# Revit family: Thorn Voyager Solid
name_source: partatom
category: Lighting Fixtures
revit_build: Autodesk Revit 2016 (Build: 20150220_1215(x64)
units: mm (PartAtom-declared; Revit-internal decimal feet)

## family parameters
Cut with Voids When Loaded = No
Host = Face
Light Source = Yes
OmniClass Number = 23.80.70.11
OmniClass Title = Luminaries for Internal Lighting
Part Type = Normal
Room Calculation Point = No
Round Connector Dimension = Use Diameter
Shared = No

## types (2) — shared parameters
Apparent Load = 2 VA
Assembly Code = D5020200
Body = Thorn_Metal_Light_Grey
Color Filter = 16777215
Cover = Thorn_PMMA_Semitransparent
Description = LED surface mount luminaire
Dimming Lamp Color Temperature Shift = <None>
Emit Shape Visible in Rendering = No
Height = 71 mm
Lamp = LED
Manufacturer = Thorn Lighting
Photometric Web File = 96629766_(STD).IES
Tilt Angle = -90.00°
Voltage = 230 V
zero-valued in all types: Default Elevation

## per-type parameters (varying)
| type | Emit from Rectangle Length | Emit from Rectangle Width | Length | Model | URL | Width |
| VOYAGER Solid L | 150 mm | 360 mm  [stored 1.1811 ft] | 360 mm  [stored 1.1811 ft] | 96629766 | www.thornlighting.com/96629766 | 150 mm |
| VOYAGER Solid MS | 130 mm  [stored 0.426509 ft] | 280 mm | 280 mm | 96629763 | www.thornlighting.com/96629763 | 130 mm  [stored 0.426509 ft] |

note: [stored X ft] marks values corroborated as IEEE doubles in the binary element streams (Revit-internal decimal feet)

## geometry (parser evidence)
native form markers: Sweep x3
no freeform markers — native parametric forms only
